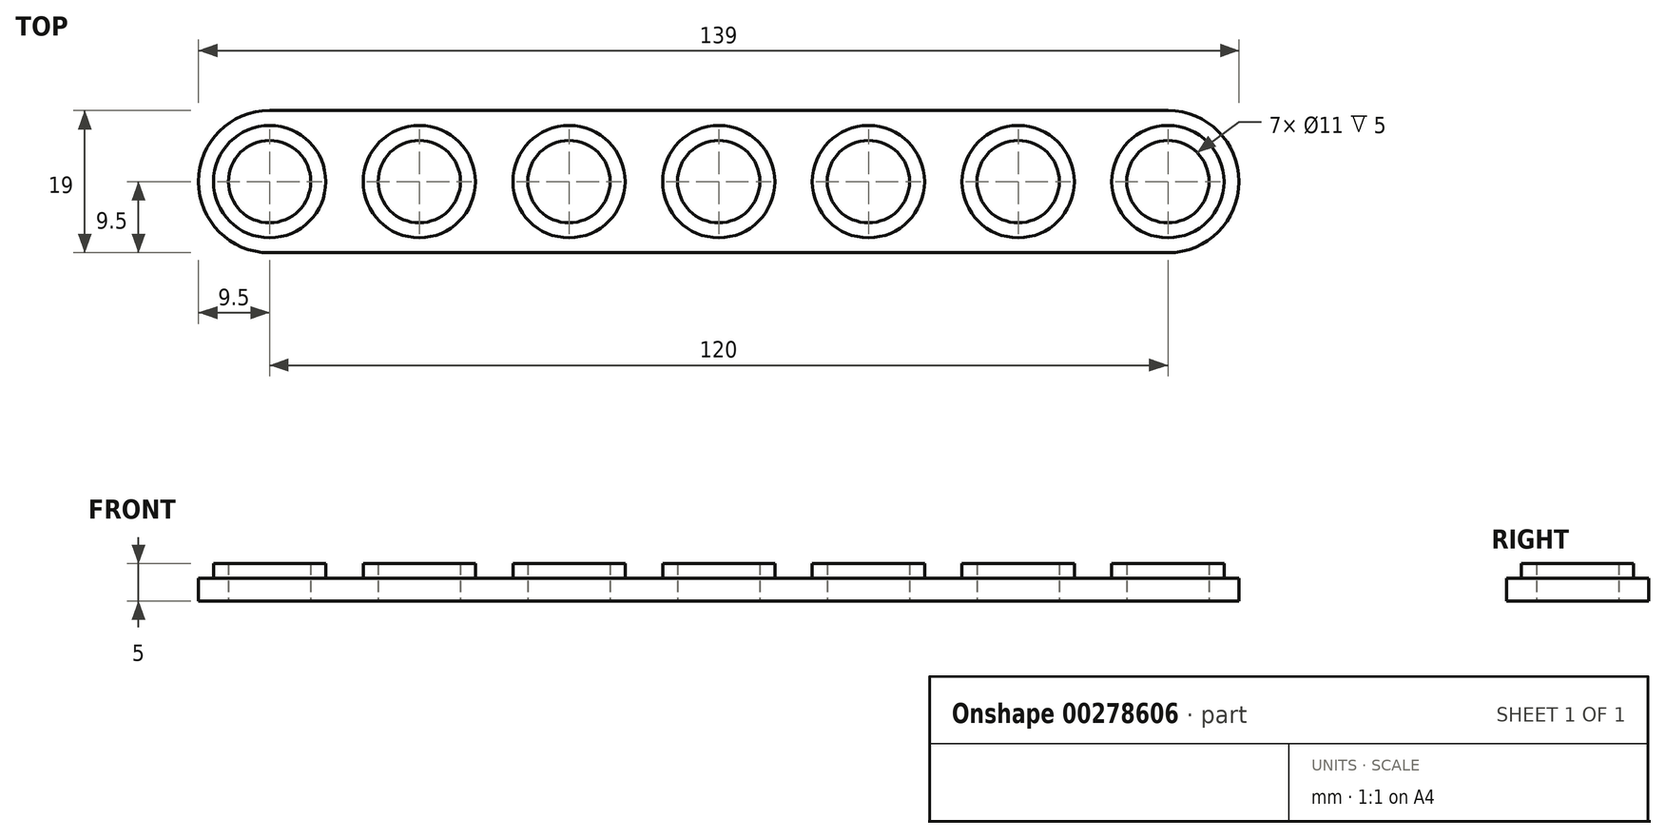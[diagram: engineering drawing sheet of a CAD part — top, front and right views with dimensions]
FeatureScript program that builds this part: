
annotation { "Feature Type Name" : "Feature", "Feature Type Description" : "" }
export const myFeature = defineFeature(function(context is Context, id is Id, definition is map)
    precondition{}
    {
        {
            assignVariable(context, id + "F0", {"name" : "e", "anyValue" : 3});
        }
        {
            assignVariable(context, id + "F1", {"name" : "h0", "anyValue" : 2});
        }
        {
            var Q0;
            Q0=qCreatedBy(makeId("Top.planeOp"),FACE);
            var sketch = newSketch(context, id + "F2", { "sketchPlane" : qUnion([Q0])});
            skLineSegment(sketch, "E0.bottom", {"start": v(0, 9.5) * mm, "end": v(120, 9.5) * mm});
            skLineSegment(sketch, "E0.top", {"start": v(0, -9.5) * mm, "end": v(120, -9.5) * mm});
            skLineSegment(sketch, "E0.left", {"start": v(-9.5, 0) * mm, "end": v(-9.5, 0) * mm});
            skLineSegment(sketch, "E0.right", {"start": v(129.5, 0) * mm, "end": v(129.5, 0) * mm});
            skPoint(sketch, "E1", {"position": v(-9.5, 0) * mm});
            skCircle(sketch, "E2", {"center": v(0, 0) * mm, "radius": 5.5 * mm});
            skPoint(sketch, "E3.visualSharp", {"position": v(129.5, 9.5) * mm});
            skArc(sketch, "E3.filletArc", {"start": v(129.5, 0) * mm, "mid": v(126.72, 6.72) * mm, "end": v(120, 9.5) * mm});
            skPoint(sketch, "E4.visualSharp", {"position": v(129.5, -9.5) * mm});
            skArc(sketch, "E4.filletArc", {"start": v(120, -9.5) * mm, "mid": v(126.72, -6.72) * mm, "end": v(129.5, 0) * mm});
            skPoint(sketch, "E5.visualSharp", {"position": v(-9.5, -9.5) * mm});
            skArc(sketch, "E5.filletArc", {"start": v(-9.5, 0) * mm, "mid": v(-6.72, -6.72) * mm, "end": v(0, -9.5) * mm});
            skPoint(sketch, "E6.visualSharp", {"position": v(-9.5, 9.5) * mm});
            skArc(sketch, "E6.filletArc", {"start": v(0, 9.5) * mm, "mid": v(-6.72, 6.72) * mm, "end": v(-9.5, 0) * mm});
            skCircle(sketch, "E7", {"center": v(0, 0) * mm, "radius": 7.5 * mm});
            skCircle(sketch, "E8.1.0.0", {"center": v(20, 0) * mm, "radius": 5.5 * mm});
            skCircle(sketch, "E8.1.0.1", {"center": v(20, 0) * mm, "radius": 7.5 * mm});
            skCircle(sketch, "E8.2.0.0", {"center": v(40, 0) * mm, "radius": 5.5 * mm});
            skCircle(sketch, "E8.2.0.1", {"center": v(40, 0) * mm, "radius": 7.5 * mm});
            skLineSegment(sketch, "E8.direction1", {"start": v(0, 0) * mm, "end": v(20, 0) * mm, "construction": true});
            skCircle(sketch, "E9.0.3.0", {"center": v(60, 0) * mm, "radius": 5.5 * mm});
            skCircle(sketch, "E9.2.3.0", {"center": v(60, 0) * mm, "radius": 7.5 * mm});
            skCircle(sketch, "E9.0.4.0", {"center": v(80, 0) * mm, "radius": 5.5 * mm});
            skCircle(sketch, "E9.2.4.0", {"center": v(80, 0) * mm, "radius": 7.5 * mm});
            skCircle(sketch, "E9.0.5.0", {"center": v(100, 0) * mm, "radius": 5.5 * mm});
            skCircle(sketch, "E9.2.5.0", {"center": v(100, 0) * mm, "radius": 7.5 * mm});
            skCircle(sketch, "E9.0.6.0", {"center": v(120, 0) * mm, "radius": 5.5 * mm});
            skCircle(sketch, "E9.2.6.0", {"center": v(120, 0) * mm, "radius": 7.5 * mm});
            skSolve(sketch);
        }
        {
            var Q0;
            Q0=qSketchRegion(id+"F2",true);
            var Q1;
            Q1=makeQuery(id+"F2.imprint","IMPRINT",FACE,{"disambiguationData":[TD([[makeQuery(id+"F2.imprint","IMPRINT",EDGE,{"derivedFrom":sQuery(id+"F2.wireOp",EDGE,"E2")}),-1.0]])]});
            var Q2;
            Q2=makeQuery(id+"F2.imprint","IMPRINT",FACE,{"disambiguationData":[TD([[makeQuery(id+"F2.imprint","IMPRINT",EDGE,{"derivedFrom":sQuery(id+"F2.wireOp",EDGE,"E8.1.0.0")}),-1.0]])]});
            var Q3;
            Q3=makeQuery(id+"F2.imprint","IMPRINT",FACE,{"disambiguationData":[TD([[makeQuery(id+"F2.imprint","IMPRINT",EDGE,{"derivedFrom":sQuery(id+"F2.wireOp",EDGE,"E8.2.0.0")}),-1.0]])]});
            var Q4;
            Q4=makeQuery(id+"F2.imprint","IMPRINT",FACE,{"disambiguationData":[TD([[makeQuery(id+"F2.imprint","IMPRINT",EDGE,{"derivedFrom":sQuery(id+"F2.wireOp",EDGE,"345b2114-0edb-480d-a68f-e22b198684d9.0.3.0")}),-1.0]])]});
            var Q5;
            Q5=makeQuery(id+"F2.imprint","IMPRINT",FACE,{"disambiguationData":[TD([[makeQuery(id+"F2.imprint","IMPRINT",EDGE,{"derivedFrom":sQuery(id+"F2.wireOp",EDGE,"E9.0.3.0")}),-1.0]])]});
            var Q6;
            Q6=makeQuery(id+"F2.imprint","IMPRINT",FACE,{"disambiguationData":[TD([[makeQuery(id+"F2.imprint","IMPRINT",EDGE,{"derivedFrom":sQuery(id+"F2.wireOp",EDGE,"E9.0.4.0")}),-1.0]])]});
            var Q7;
            Q7=makeQuery(id+"F2.imprint","IMPRINT",FACE,{"disambiguationData":[TD([[makeQuery(id+"F2.imprint","IMPRINT",EDGE,{"derivedFrom":sQuery(id+"F2.wireOp",EDGE,"E9.0.5.0")}),-1.0]])]});
            var Q8;
            Q8=makeQuery(id+"F2.imprint","IMPRINT",FACE,{"disambiguationData":[TD([[makeQuery(id+"F2.imprint","IMPRINT",EDGE,{"derivedFrom":sQuery(id+"F2.wireOp",EDGE,"E9.0.6.0")}),-1.0]])]});
            var Q9;
            Q9=makeQuery(id+"F2.imprint","IMPRINT",FACE,{"disambiguationData":[TD([[makeQuery(id+"F2.imprint","IMPRINT",EDGE,{"derivedFrom":sQuery(id+"F2.wireOp",EDGE,"E9.0.7.0")}),-1.0]])]});
            var Q10;
            Q10=makeQuery(id+"F2.imprint","IMPRINT",FACE,{"disambiguationData":[TD([[makeQuery(id+"F2.imprint","IMPRINT",EDGE,{"derivedFrom":sQuery(id+"F2.wireOp",EDGE,"E9.0.8.0")}),-1.0]])]});
            var Q11;
            Q11=makeQuery(id+"F2.imprint","IMPRINT",FACE,{"disambiguationData":[TD([[makeQuery(id+"F2.imprint","IMPRINT",EDGE,{"derivedFrom":sQuery(id+"F2.wireOp",EDGE,"E9.0.9.0")}),-1.0]])]});
            extrude(context, id + "F3", {"entities" : qUnion([Q0, Q1, Q2, Q3, Q4, Q5, Q6, Q7, Q8, Q9, Q10, Q11]), "depth" : (getVariable(context, 'e')) * mm});
        }
        {
            var Q0;
            Q0=makeQuery(id+"F2.imprint","IMPRINT",FACE,{"disambiguationData":[TD([[makeQuery(id+"F2.imprint","IMPRINT",EDGE,{"derivedFrom":sQuery(id+"F2.wireOp",EDGE,"E2")}),-1.0]])]});
            var Q1;
            Q1=makeQuery(id+"F2.imprint","IMPRINT",FACE,{"disambiguationData":[TD([[makeQuery(id+"F2.imprint","IMPRINT",EDGE,{"derivedFrom":sQuery(id+"F2.wireOp",EDGE,"E8.1.0.0")}),-1.0]])]});
            var Q2;
            Q2=makeQuery(id+"F2.imprint","IMPRINT",FACE,{"disambiguationData":[TD([[makeQuery(id+"F2.imprint","IMPRINT",EDGE,{"derivedFrom":sQuery(id+"F2.wireOp",EDGE,"E8.2.0.0")}),-1.0]])]});
            var Q3;
            Q3=makeQuery(id+"F2.imprint","IMPRINT",FACE,{"disambiguationData":[TD([[makeQuery(id+"F2.imprint","IMPRINT",EDGE,{"derivedFrom":sQuery(id+"F2.wireOp",EDGE,"345b2114-0edb-480d-a68f-e22b198684d9.0.3.0")}),-1.0]])]});
            var Q4;
            Q4=makeQuery(id+"F2.imprint","IMPRINT",FACE,{"disambiguationData":[TD([[makeQuery(id+"F2.imprint","IMPRINT",EDGE,{"derivedFrom":sQuery(id+"F2.wireOp",EDGE,"E9.0.3.0")}),-1.0]])]});
            var Q5;
            Q5=makeQuery(id+"F2.imprint","IMPRINT",FACE,{"disambiguationData":[TD([[makeQuery(id+"F2.imprint","IMPRINT",EDGE,{"derivedFrom":sQuery(id+"F2.wireOp",EDGE,"E9.0.4.0")}),-1.0]])]});
            var Q6;
            Q6=makeQuery(id+"F2.imprint","IMPRINT",FACE,{"disambiguationData":[TD([[makeQuery(id+"F2.imprint","IMPRINT",EDGE,{"derivedFrom":sQuery(id+"F2.wireOp",EDGE,"E9.0.5.0")}),-1.0]])]});
            var Q7;
            Q7=makeQuery(id+"F2.imprint","IMPRINT",FACE,{"disambiguationData":[TD([[makeQuery(id+"F2.imprint","IMPRINT",EDGE,{"derivedFrom":sQuery(id+"F2.wireOp",EDGE,"E9.0.6.0")}),-1.0]])]});
            var Q8;
            Q8=makeQuery(id+"F2.imprint","IMPRINT",FACE,{"disambiguationData":[TD([[makeQuery(id+"F2.imprint","IMPRINT",EDGE,{"derivedFrom":sQuery(id+"F2.wireOp",EDGE,"E9.0.7.0")}),-1.0]])]});
            var Q9;
            Q9=makeQuery(id+"F2.imprint","IMPRINT",FACE,{"disambiguationData":[TD([[makeQuery(id+"F2.imprint","IMPRINT",EDGE,{"derivedFrom":sQuery(id+"F2.wireOp",EDGE,"E9.0.8.0")}),-1.0]])]});
            var Q10;
            Q10=makeQuery(id+"F2.imprint","IMPRINT",FACE,{"disambiguationData":[TD([[makeQuery(id+"F2.imprint","IMPRINT",EDGE,{"derivedFrom":sQuery(id+"F2.wireOp",EDGE,"E9.0.9.0")}),-1.0]])]});
            extrude(context, id + "F4", {"entities" : qUnion([Q0, Q1, Q2, Q3, Q4, Q5, Q6, Q7, Q8, Q9, Q10]), "operationType" : NewBodyOperationType.ADD, "depth" : (getVariable(context, 'e') + getVariable(context, 'h0')) * mm});
        }
    });
